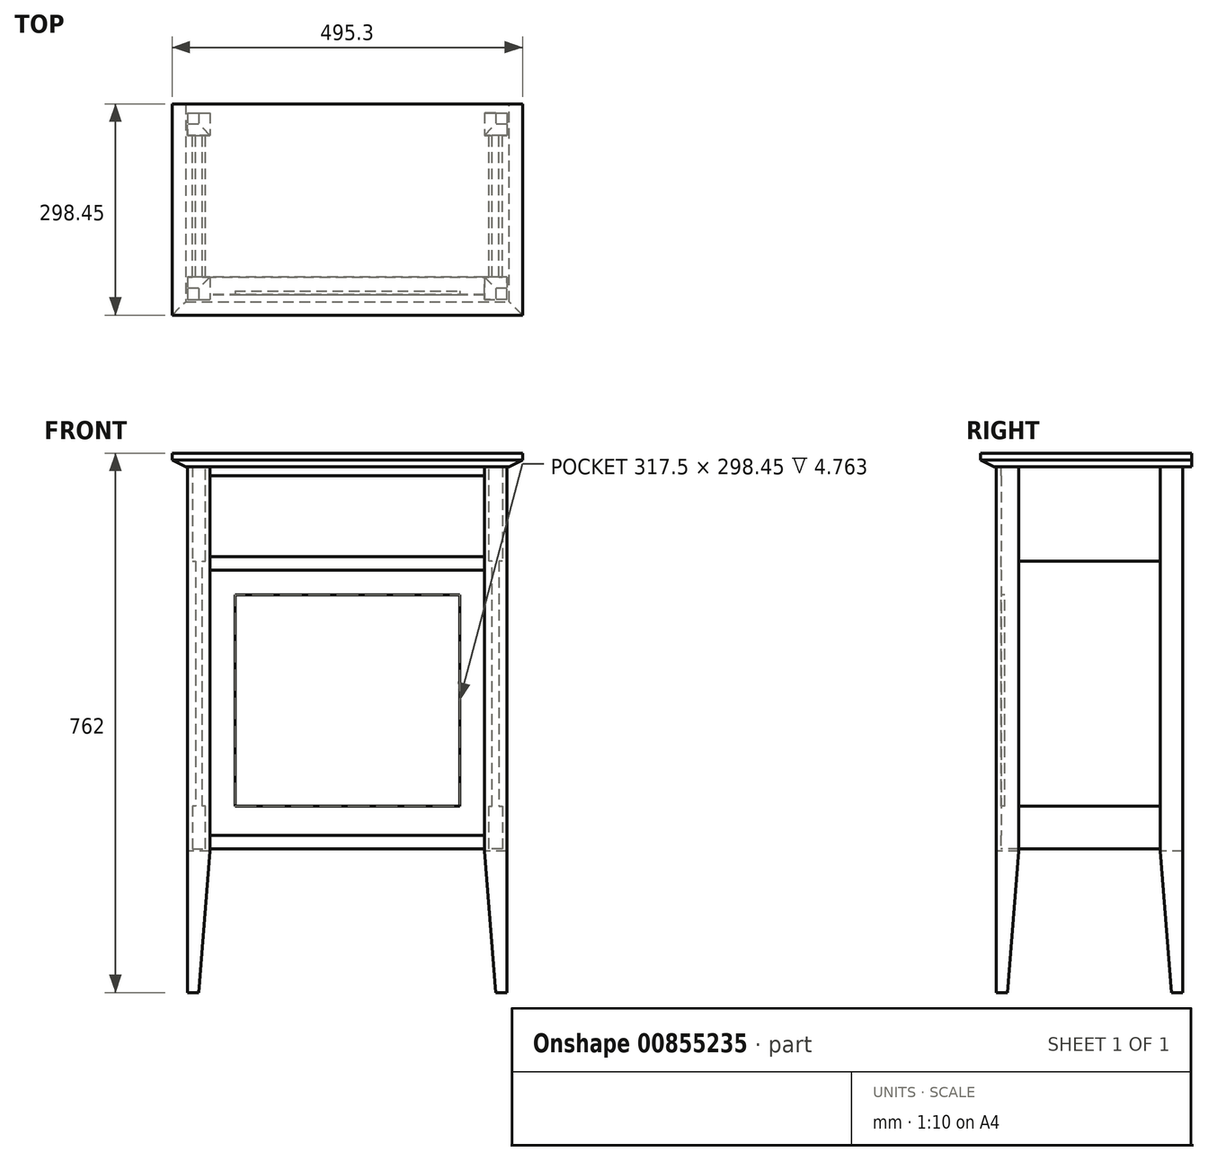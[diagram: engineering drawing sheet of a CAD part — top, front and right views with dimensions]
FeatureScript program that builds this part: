
annotation { "Feature Type Name" : "Feature", "Feature Type Description" : "" }
export const myFeature = defineFeature(function(context is Context, id is Id, definition is map)
    precondition{}
    {
        {
            var Q0;
            Q0=qCreatedBy(makeId("Top.planeOp"),FACE);
            var sketch = newSketch(context, id + "F0", { "sketchPlane" : qUnion([Q0])});
            skLineSegment(sketch, "E0", {"start": v(-209.55, 115.89) * mm, "end": v(209.55, 115.89) * mm, "construction": true});
            skLineSegment(sketch, "E1", {"start": v(209.55, 115.89) * mm, "end": v(209.55, -115.89) * mm, "construction": true});
            skLineSegment(sketch, "E2", {"start": v(209.55, -115.89) * mm, "end": v(-209.55, -115.89) * mm, "construction": true});
            skLineSegment(sketch, "E3", {"start": v(-209.55, -115.89) * mm, "end": v(-209.55, 115.89) * mm, "construction": true});
            skLineSegment(sketch, "E4", {"start": v(0, 115.89) * mm, "end": v(0, -115.89) * mm, "construction": true});
            skLineSegment(sketch, "E5", {"start": v(-209.55, 0) * mm, "end": v(209.55, 0) * mm, "construction": true});
            skPoint(sketch, "E6", {"position": v(0, 0) * mm});
            skLineSegment(sketch, "E7.bottom", {"start": v(-225.43, 131.76) * mm, "end": v(-193.68, 131.76) * mm});
            skLineSegment(sketch, "E7.top", {"start": v(-225.43, 100.01) * mm, "end": v(-193.68, 100.01) * mm});
            skLineSegment(sketch, "E7.left", {"start": v(-225.43, 131.76) * mm, "end": v(-225.43, 100.01) * mm});
            skLineSegment(sketch, "E7.right", {"start": v(-193.68, 131.76) * mm, "end": v(-193.68, 100.01) * mm});
            skPoint(sketch, "E7.middle", {"position": v(-209.55, 115.89) * mm});
            skLineSegment(sketch, "E8.bottom", {"start": v(193.67, 131.76) * mm, "end": v(225.42, 131.76) * mm});
            skLineSegment(sketch, "E8.top", {"start": v(193.67, 100.01) * mm, "end": v(225.42, 100.01) * mm});
            skLineSegment(sketch, "E8.left", {"start": v(193.67, 131.76) * mm, "end": v(193.67, 100.01) * mm});
            skLineSegment(sketch, "E8.right", {"start": v(225.42, 131.76) * mm, "end": v(225.42, 100.01) * mm});
            skPoint(sketch, "E8.middle", {"position": v(209.55, 115.89) * mm});
            skLineSegment(sketch, "E9.bottom", {"start": v(-225.42, -100.01) * mm, "end": v(-193.67, -100.01) * mm});
            skLineSegment(sketch, "E9.top", {"start": v(-225.42, -131.76) * mm, "end": v(-193.67, -131.76) * mm});
            skLineSegment(sketch, "E9.left", {"start": v(-225.42, -100.01) * mm, "end": v(-225.42, -131.76) * mm});
            skLineSegment(sketch, "E9.right", {"start": v(-193.67, -100.01) * mm, "end": v(-193.67, -131.76) * mm});
            skPoint(sketch, "E9.middle", {"position": v(-209.55, -115.89) * mm});
            skLineSegment(sketch, "E10.bottom", {"start": v(225.43, -131.76) * mm, "end": v(193.68, -131.76) * mm});
            skLineSegment(sketch, "E10.top", {"start": v(225.43, -100.01) * mm, "end": v(193.68, -100.01) * mm});
            skLineSegment(sketch, "E10.left", {"start": v(225.43, -131.76) * mm, "end": v(225.43, -100.01) * mm});
            skLineSegment(sketch, "E10.right", {"start": v(193.68, -131.76) * mm, "end": v(193.68, -100.01) * mm});
            skPoint(sketch, "E10.middle", {"position": v(209.55, -115.89) * mm});
            skSolve(sketch);
        }
        {
            var Q0;
            Q0=qSketchRegion(id+"F0",true);
            extrude(context, id + "F1", {"entities" : qUnion([Q0]), "depth" : 742.95 * mm, "offsetDistance" : 25.4 * mm});
        }
        {
            var Q0;
            Q0=makeQuery(id+"F1.opExtrude","SWEPT_FACE",FACE,{"disambiguationData":[OSD([sQuery(id+"F0.wireOp",EDGE,"E7.top")])]});
            var sketch = newSketch(context, id + "F2", { "sketchPlane" : qUnion([Q0])});
            skLineSegment(sketch, "E11", {"start": v(-209.55, 742.95) * mm, "end": v(-209.55, 0) * mm, "construction": true});
            skLineSegment(sketch, "E12", {"start": v(-219.08, 742.95) * mm, "end": v(-219.08, 609.6) * mm});
            skLineSegment(sketch, "E13", {"start": v(-219.08, 609.6) * mm, "end": v(-200.03, 609.6) * mm});
            skLineSegment(sketch, "E14", {"start": v(-200.03, 609.6) * mm, "end": v(-200.03, 742.95) * mm});
            skLineSegment(sketch, "E15", {"start": v(-200.03, 742.95) * mm, "end": v(-219.08, 742.95) * mm});
            skLineSegment(sketch, "E16", {"start": v(-214.31, 609.6) * mm, "end": v(-214.31, 263.53) * mm});
            skLineSegment(sketch, "E17", {"start": v(-214.31, 263.53) * mm, "end": v(-204.79, 263.53) * mm});
            skLineSegment(sketch, "E18", {"start": v(-204.79, 263.53) * mm, "end": v(-204.79, 609.6) * mm});
            skLineSegment(sketch, "E19", {"start": v(-219.08, 263.53) * mm, "end": v(-219.08, 203.2) * mm});
            skLineSegment(sketch, "E20", {"start": v(-219.08, 203.2) * mm, "end": v(-200.03, 203.2) * mm});
            skLineSegment(sketch, "E21", {"start": v(-200.03, 203.2) * mm, "end": v(-200.03, 263.53) * mm});
            skLineSegment(sketch, "E22", {"start": v(-200.03, 263.53) * mm, "end": v(-219.08, 263.53) * mm});
            skLineSegment(sketch, "E23", {"start": v(-193.68, 0) * mm, "end": v(-193.68, 200.03) * mm});
            skLineSegment(sketch, "E24", {"start": v(-193.68, 200.03) * mm, "end": v(-209.55, 0) * mm});
            skLineSegment(sketch, "E25", {"start": v(-209.55, 0) * mm, "end": v(-193.68, 0) * mm});
            skLineSegment(sketch, "E26", {"start": v(0, 0) * mm, "end": v(0, 787.82) * mm, "construction": true});
            skLineSegment(sketch, "E27.MirrorCS", {"start": v(200.03, 742.95) * mm, "end": v(219.08, 742.95) * mm});
            skLineSegment(sketch, "E28.MirrorCS", {"start": v(219.08, 742.95) * mm, "end": v(219.08, 609.6) * mm});
            skLineSegment(sketch, "E29.MirrorCS", {"start": v(200.03, 609.6) * mm, "end": v(200.03, 742.95) * mm});
            skLineSegment(sketch, "E30.MirrorCS", {"start": v(219.08, 609.6) * mm, "end": v(200.03, 609.6) * mm});
            skLineSegment(sketch, "E31.MirrorCS", {"start": v(214.31, 609.6) * mm, "end": v(214.31, 263.53) * mm});
            skLineSegment(sketch, "E32.MirrorCS", {"start": v(204.79, 263.53) * mm, "end": v(204.79, 609.6) * mm});
            skLineSegment(sketch, "E33.MirrorCS", {"start": v(200.03, 263.53) * mm, "end": v(219.08, 263.53) * mm});
            skLineSegment(sketch, "E34.MirrorCS", {"start": v(219.08, 263.53) * mm, "end": v(219.08, 203.2) * mm});
            skLineSegment(sketch, "E35.MirrorCS", {"start": v(200.03, 203.2) * mm, "end": v(200.03, 263.53) * mm});
            skLineSegment(sketch, "E36.MirrorCS", {"start": v(219.08, 203.2) * mm, "end": v(200.03, 203.2) * mm});
            skLineSegment(sketch, "E37.MirrorCS", {"start": v(193.68, 200.03) * mm, "end": v(209.55, 0) * mm});
            skLineSegment(sketch, "E38.MirrorCS", {"start": v(193.68, 0) * mm, "end": v(193.68, 200.03) * mm});
            skLineSegment(sketch, "E39.MirrorCS", {"start": v(209.55, 0) * mm, "end": v(193.68, 0) * mm});
            skSolve(sketch);
        }
        {
            var Q0;
            {var subQ3=sQuery(id+"F2.wireOp",EDGE,"E19");Q0=makeQuery(id+"F2.imprint","IMPRINT",FACE,{"disambiguationData":[TD([[makeQuery(id+"F2.imprint","IMPRINT",EDGE,{"derivedFrom":subQ3}),1.0]])]});}
            var Q1;
            {var subQ0=sQuery(id+"F2.wireOp",EDGE,"E16");Q1=makeQuery(id+"F2.imprint","IMPRINT",FACE,{"disambiguationData":[TD([[makeQuery(id+"F2.imprint","IMPRINT",EDGE,{"derivedFrom":subQ0}),1.0]])]});}
            var Q2;
            {var subQ4=sQuery(id+"F2.wireOp",EDGE,"E12");Q2=makeQuery(id+"F2.imprint","IMPRINT",FACE,{"disambiguationData":[TD([[makeQuery(id+"F2.imprint","IMPRINT",EDGE,{"derivedFrom":subQ4}),1.0]])]});}
            var Q3;
            Q3=makeQuery(id+"F2.imprint","IMPRINT",FACE,{"disambiguationData":[TD([[makeQuery(id+"F2.imprint","IMPRINT",EDGE,{"derivedFrom":sQuery(id+"F2.wireOp",EDGE,"E27.MirrorCS")}),-1.0]])]});
            var Q4;
            {var subQ0=sQuery(id+"F2.wireOp",EDGE,"E31.MirrorCS");Q4=makeQuery(id+"F2.imprint","IMPRINT",FACE,{"disambiguationData":[TD([[makeQuery(id+"F2.imprint","IMPRINT",EDGE,{"derivedFrom":subQ0}),-1.0]])]});}
            var Q5;
            {var subQ0=sQuery(id+"F2.wireOp",EDGE,"E34.MirrorCS");Q5=makeQuery(id+"F2.imprint","IMPRINT",FACE,{"disambiguationData":[TD([[makeQuery(id+"F2.imprint","IMPRINT",EDGE,{"derivedFrom":subQ0}),-1.0]])]});}
            extrude(context, id + "F3", {"entities" : qUnion([Q0, Q1, Q2, Q3, Q4, Q5]), "operationType" : NewBodyOperationType.ADD, "endBound" : BoundingType.UP_TO_NEXT, "depth" : 25.4 * mm, "offsetDistance" : 25.4 * mm});
        }
        {
            var Q0;
            Q0=makeQuery(id+"F2.imprint","IMPRINT",FACE,{"disambiguationData":[TD([[makeQuery(id+"F2.imprint","IMPRINT",EDGE,{"derivedFrom":sQuery(id+"F2.wireOp",EDGE,"E23")}),-1.0]])]});
            var Q1;
            Q1=makeQuery(id+"F2.imprint","IMPRINT",FACE,{"disambiguationData":[TD([[makeQuery(id+"F2.imprint","IMPRINT",EDGE,{"derivedFrom":sQuery(id+"F2.wireOp",EDGE,"E37.MirrorCS")}),-1.0]])]});
            extrude(context, id + "F4", {"entities" : qUnion([Q0, Q1]), "operationType" : NewBodyOperationType.REMOVE, "endBound" : BoundingType.THROUGH_ALL, "oppositeDirection" : true, "depth" : 25.4 * mm, "offsetDistance" : 25.4 * mm, "hasSecondDirection" : true, "secondDirectionBound" : SecondDirectionBoundingType.THROUGH_ALL, "secondDirectionOppositeDirection" : false, "secondDirectionDepth" : 25.4 * mm});
        }
        {
            var Q0;
            Q0=makeQuery(id+"F1.opExtrude","SWEPT_FACE",FACE,{"disambiguationData":[OSD([sQuery(id+"F0.wireOp",EDGE,"E9.left")])]});
            var sketch = newSketch(context, id + "F5", { "sketchPlane" : qUnion([Q0])});
            skLineSegment(sketch, "E40", {"start": v(100.01, 200.03) * mm, "end": v(115.89, 0) * mm});
            skLineSegment(sketch, "E41", {"start": v(115.89, 0) * mm, "end": v(100.01, 0) * mm});
            skLineSegment(sketch, "E42", {"start": v(100.01, 0) * mm, "end": v(100.01, 200.03) * mm});
            skLineSegment(sketch, "E43", {"start": v(0, 0) * mm, "end": v(0, 281.06) * mm, "construction": true});
            skLineSegment(sketch, "E44.MirrorCS", {"start": v(-100.01, 200.03) * mm, "end": v(-115.89, 0) * mm});
            skLineSegment(sketch, "E45.MirrorCS", {"start": v(-100.01, 0) * mm, "end": v(-100.01, 200.03) * mm});
            skLineSegment(sketch, "E46.MirrorCS", {"start": v(-115.89, 0) * mm, "end": v(-100.01, 0) * mm});
            skSolve(sketch);
        }
        {
            var Q0;
            Q0=qSketchRegion(id+"F5",true);
            extrude(context, id + "F6", {"entities" : qUnion([Q0]), "operationType" : NewBodyOperationType.REMOVE, "endBound" : BoundingType.THROUGH_ALL, "oppositeDirection" : true, "depth" : 25.4 * mm, "offsetDistance" : 25.4 * mm});
        }
        {
            var Q0;
            Q0=makeQuery(id+"F1.opExtrude","SWEPT_FACE",FACE,{"disambiguationData":[OSD([sQuery(id+"F0.wireOp",EDGE,"E9.right")])]});
            var sketch = newSketch(context, id + "F7", { "sketchPlane" : qUnion([Q0])});
            skLineSegment(sketch, "E47.bottom", {"start": v(-100.01, 742.95) * mm, "end": v(-125.41, 742.95) * mm});
            skLineSegment(sketch, "E47.top", {"start": v(-100.01, 730.25) * mm, "end": v(-125.41, 730.25) * mm});
            skLineSegment(sketch, "E47.left", {"start": v(-100.01, 742.95) * mm, "end": v(-100.01, 730.25) * mm});
            skLineSegment(sketch, "E47.right", {"start": v(-125.41, 742.95) * mm, "end": v(-125.41, 730.25) * mm});
            skLineSegment(sketch, "E48.bottom", {"start": v(-100.01, 615.95) * mm, "end": v(-125.41, 615.95) * mm});
            skLineSegment(sketch, "E48.top", {"start": v(-100.01, 596.9) * mm, "end": v(-125.41, 596.9) * mm});
            skLineSegment(sketch, "E48.left", {"start": v(-100.01, 615.95) * mm, "end": v(-100.01, 596.9) * mm});
            skLineSegment(sketch, "E48.right", {"start": v(-125.41, 615.95) * mm, "end": v(-125.41, 596.9) * mm});
            skLineSegment(sketch, "E49", {"start": v(-125.02, 730.25) * mm, "end": v(-125.02, 615.95) * mm});
            skLineSegment(sketch, "E50", {"start": v(-100.01, 615.95) * mm, "end": v(-100.01, 730.25) * mm});
            skLineSegment(sketch, "E51.bottom", {"start": v(-100.01, 222.25) * mm, "end": v(-125.41, 222.25) * mm});
            skLineSegment(sketch, "E51.top", {"start": v(-100.01, 203.2) * mm, "end": v(-125.41, 203.2) * mm});
            skLineSegment(sketch, "E51.left", {"start": v(-100.01, 222.25) * mm, "end": v(-100.01, 203.2) * mm});
            skLineSegment(sketch, "E51.right", {"start": v(-125.41, 222.25) * mm, "end": v(-125.41, 203.2) * mm});
            skLineSegment(sketch, "E52", {"start": v(-125.02, 596.9) * mm, "end": v(-125.02, 222.25) * mm});
            skLineSegment(sketch, "E53", {"start": v(-100.01, 222.25) * mm, "end": v(-100.01, 596.9) * mm});
            skSolve(sketch);
        }
        {
            var Q0;
            Q0=qSketchRegion(id+"F7",true);
            extrude(context, id + "F8", {"entities" : qUnion([Q0]), "operationType" : NewBodyOperationType.ADD, "endBound" : BoundingType.UP_TO_NEXT, "depth" : 25.4 * mm, "offsetDistance" : 25.4 * mm});
        }
        {
            var Q0;
            Q0=makeQuery(id+"F8.opExtrude","SWEPT_FACE",FACE,{"disambiguationData":[OSD([sQuery(id+"F7.wireOp",EDGE,"E52")])]});
            var sketch = newSketch(context, id + "F9", { "sketchPlane" : qUnion([Q0])});
            skLineSegment(sketch, "E54.0", {"start": v(-158.75, 257.18) * mm, "end": v(158.75, 257.18) * mm});
            skLineSegment(sketch, "E54.1", {"start": v(-158.75, 561.98) * mm, "end": v(-158.75, 257.18) * mm});
            skLineSegment(sketch, "E54.2", {"start": v(158.75, 561.98) * mm, "end": v(-158.75, 561.98) * mm});
            skLineSegment(sketch, "E54.3", {"start": v(158.75, 257.18) * mm, "end": v(158.75, 561.98) * mm});
            skLineSegment(sketch, "E55", {"start": v(-158.75, 263.53) * mm, "end": v(158.75, 263.53) * mm});
            skSolve(sketch);
        }
        {
            var Q0;
            {var subQ0=sQuery(id+"F9.wireOp",EDGE,"E54.2");Q0=makeQuery(id+"F9.imprint","IMPRINT",FACE,{"disambiguationData":[TD([[makeQuery(id+"F9.imprint","IMPRINT",EDGE,{"derivedFrom":subQ0}),1.0]])]});}
            extrude(context, id + "F10", {"entities" : qUnion([Q0]), "operationType" : NewBodyOperationType.REMOVE, "oppositeDirection" : true, "depth" : 4.76 * mm, "offsetDistance" : 25.4 * mm});
        }
        {
            var Q0;
            Q0=makeQuery(id+"F8.boolean.opBoolean","MERGE",FACE,{"derivedFrom":[makeQuery(id+"F3.boolean.opBoolean","MERGE",FACE,{"derivedFrom":[makeQuery(id+"F1.opExtrude","CAP_FACE",FACE,{"disambiguationData":[OSD([sQuery(id+"F0.wireOp",EDGE,"E7.bottom"),sQuery(id+"F0.wireOp",EDGE,"E7.top"),sQuery(id+"F0.wireOp",EDGE,"E7.left"),sQuery(id+"F0.wireOp",EDGE,"E7.right")])],"isStart":false}),makeQuery(id+"F1.opExtrude","CAP_FACE",FACE,{"disambiguationData":[OSD([sQuery(id+"F0.wireOp",EDGE,"E9.bottom"),sQuery(id+"F0.wireOp",EDGE,"E9.top"),sQuery(id+"F0.wireOp",EDGE,"E9.left"),sQuery(id+"F0.wireOp",EDGE,"E9.right")])],"isStart":false}),makeQuery(id+"F3.opExtrude","SWEPT_FACE",FACE,{"disambiguationData":[OSD([sQuery(id+"F2.wireOp",EDGE,"E15")])]})]}),makeQuery(id+"F3.boolean.opBoolean","MERGE",FACE,{"derivedFrom":[makeQuery(id+"F1.opExtrude","CAP_FACE",FACE,{"disambiguationData":[OSD([sQuery(id+"F0.wireOp",EDGE,"E8.bottom"),sQuery(id+"F0.wireOp",EDGE,"E8.top"),sQuery(id+"F0.wireOp",EDGE,"E8.left"),sQuery(id+"F0.wireOp",EDGE,"E8.right")])],"isStart":false}),makeQuery(id+"F1.opExtrude","CAP_FACE",FACE,{"disambiguationData":[OSD([sQuery(id+"F0.wireOp",EDGE,"E10.bottom"),sQuery(id+"F0.wireOp",EDGE,"E10.top"),sQuery(id+"F0.wireOp",EDGE,"E10.left"),sQuery(id+"F0.wireOp",EDGE,"E10.right")])],"isStart":false}),makeQuery(id+"F3.opExtrude","SWEPT_FACE",FACE,{"disambiguationData":[OSD([sQuery(id+"F2.wireOp",EDGE,"E27.MirrorCS")])]})]}),makeQuery(id+"F8.opExtrude","SWEPT_FACE",FACE,{"disambiguationData":[OSD([sQuery(id+"F7.wireOp",EDGE,"E47.bottom")])]})]});
            var sketch = newSketch(context, id + "F11", { "sketchPlane" : qUnion([Q0])});
            skLineSegment(sketch, "E56", {"start": v(0, 137.26) * mm, "end": v(0, -185.37) * mm, "construction": true});
            skLineSegment(sketch, "E57", {"start": v(-177.63, 0) * mm, "end": v(186.24, 0) * mm, "construction": true});
            skLineSegment(sketch, "E58", {"start": v(-247.65, 144.46) * mm, "end": v(247.65, 144.46) * mm});
            skLineSegment(sketch, "E59", {"start": v(247.65, 144.46) * mm, "end": v(247.65, -153.99) * mm});
            skLineSegment(sketch, "E60", {"start": v(247.65, -153.99) * mm, "end": v(-247.65, -153.99) * mm});
            skLineSegment(sketch, "E61", {"start": v(-247.65, -153.99) * mm, "end": v(-247.65, 144.46) * mm});
            skSolve(sketch);
        }
        {
            var Q0;
            Q0=qSketchRegion(id+"F11",true);
            extrude(context, id + "F12", {"entities" : qUnion([Q0]), "operationType" : NewBodyOperationType.ADD, "depth" : 19.05 * mm, "offsetDistance" : 25.4 * mm});
        }
        {
            var Q0;
            Q0=makeQuery(id+"F12.opExtrude","SWEPT_FACE",FACE,{"disambiguationData":[OSD([sQuery(id+"F11.wireOp",EDGE,"E58")])]});
            var sketch = newSketch(context, id + "F13", { "sketchPlane" : qUnion([Q0])});
            skLineSegment(sketch, "E62", {"start": v(228.6, 742.95) * mm, "end": v(247.65, 752.48) * mm});
            skLineSegment(sketch, "E63", {"start": v(247.65, 752.48) * mm, "end": v(247.65, 742.95) * mm});
            skLineSegment(sketch, "E64", {"start": v(247.65, 742.95) * mm, "end": v(228.6, 742.95) * mm});
            skSolve(sketch);
        }
        {
            var Q0;
            Q0=makeQuery(id+"F13.imprint","IMPRINT",FACE,{"disambiguationData":[TD([[makeQuery(id+"F13.imprint","IMPRINT",EDGE,{"derivedFrom":sQuery(id+"F13.wireOp",EDGE,"E62")}),-1.0]])]});
            var Q1;
            Q1=makeQuery(id+"F1NDxMYOyf2uWx9_1.boolean.opBoolean","MERGE",EDGE,{"derivedFrom":[makeQuery(id+"F12.opExtrude","CAP_EDGE",EDGE,{"disambiguationData":[OSD([sQuery(id+"F11.wireOp",EDGE,"E61")])],"isStart":true}),makeQuery(id+"F1NDxMYOyf2uWx9_1.opExtrude","SWEPT_EDGE",EDGE,{"disambiguationData":[OSD([sQuery(id+"F13.wireOp",EDGE,"E63"),sQuery(id+"F13.wireOp",EDGE,"E64")])]})]});
            var Q2;
            Q2=makeQuery(id+"F12.opExtrude","CAP_EDGE",EDGE,{"disambiguationData":[OSD([sQuery(id+"F11.wireOp",EDGE,"E60")])],"isStart":true});
            var Q3;
            Q3=makeQuery(id+"F12.opExtrude","CAP_EDGE",EDGE,{"disambiguationData":[OSD([sQuery(id+"F11.wireOp",EDGE,"E59")])],"isStart":true});
            sweep(context, id + "F14", {"operationType" : NewBodyOperationType.REMOVE, "profiles" : qUnion([Q0]), "path" : qUnion([Q1, Q2, Q3])});
        }
    });
